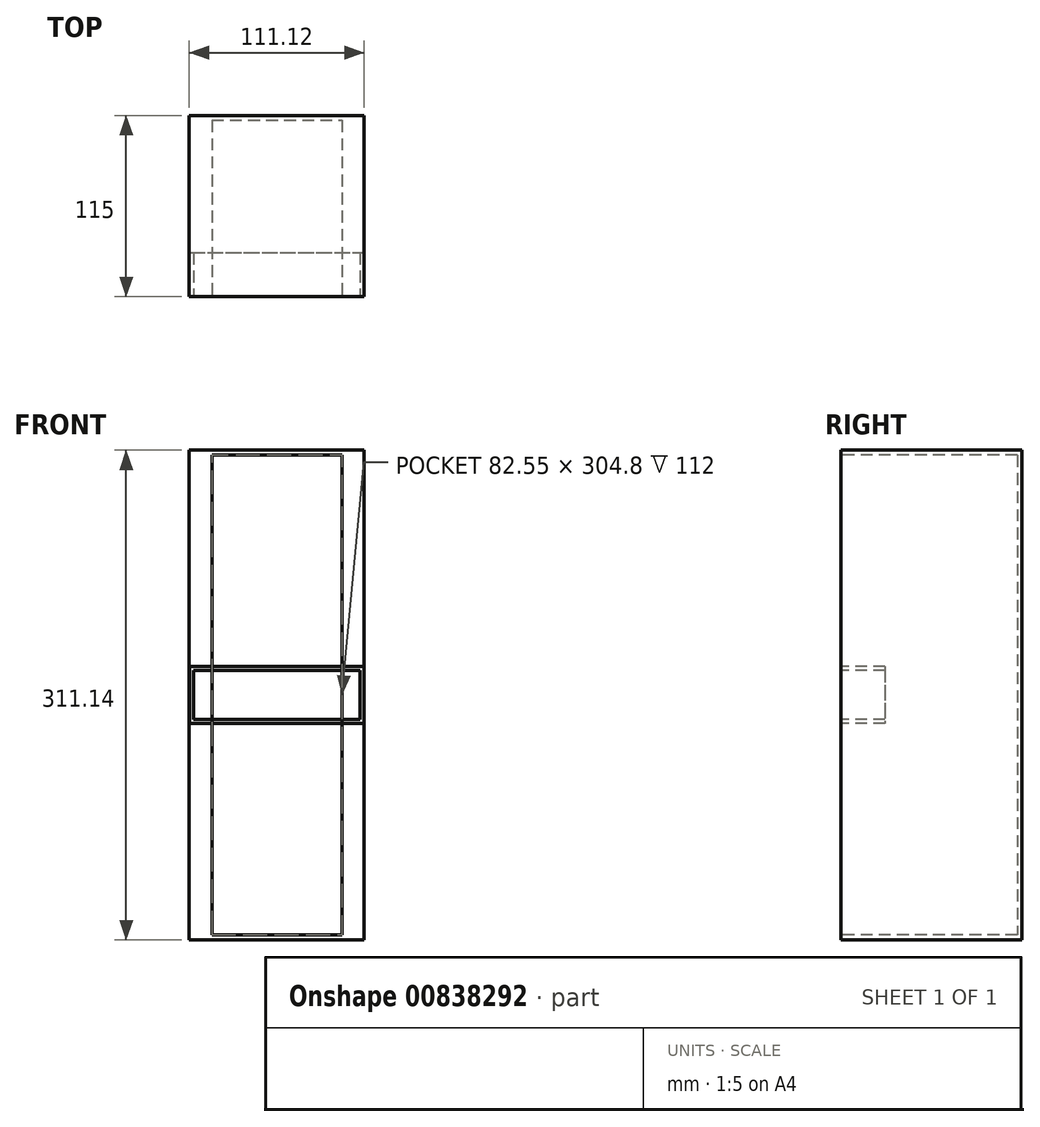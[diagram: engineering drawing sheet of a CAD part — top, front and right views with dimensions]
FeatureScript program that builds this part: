
annotation { "Feature Type Name" : "Feature", "Feature Type Description" : "" }
export const myFeature = defineFeature(function(context is Context, id is Id, definition is map)
    precondition{}
    {
        {
            var Q0;
            Q0=qCreatedBy(makeId("Front.planeOp"),FACE);
            var sketch = newSketch(context, id + "F0", { "sketchPlane" : qUnion([Q0])});
            skLineSegment(sketch, "E0.bottom", {"start": v(-55.56, 155.58) * mm, "end": v(55.56, 155.58) * mm});
            skLineSegment(sketch, "E0.top", {"start": v(-55.56, -155.58) * mm, "end": v(55.56, -155.58) * mm});
            skLineSegment(sketch, "E0.left", {"start": v(-55.56, 155.58) * mm, "end": v(-55.56, -155.58) * mm});
            skLineSegment(sketch, "E0.right", {"start": v(55.56, 155.58) * mm, "end": v(55.56, -155.58) * mm});
            skPoint(sketch, "E0.middle", {"position": v(0, 0) * mm});
            skSolve(sketch);
        }
        {
            var Q0;
            Q0=qCreatedBy(makeId("Front.planeOp"),FACE);
            var sketch = newSketch(context, id + "F1", { "sketchPlane" : qUnion([Q0])});
            skLineSegment(sketch, "E1.bottom", {"start": v(-41.28, 152.4) * mm, "end": v(41.27, 152.4) * mm});
            skLineSegment(sketch, "E1.top", {"start": v(-41.27, -152.4) * mm, "end": v(41.28, -152.4) * mm});
            skLineSegment(sketch, "E1.left", {"start": v(-41.28, 152.4) * mm, "end": v(-41.27, -152.4) * mm});
            skLineSegment(sketch, "E1.right", {"start": v(41.27, 152.4) * mm, "end": v(41.28, -152.4) * mm});
            skPoint(sketch, "E1.middle", {"position": v(0, 0) * mm});
            skSolve(sketch);
        }
        {
            var Q0;
            Q0=makeQuery(id+"F0.imprint","IMPRINT",FACE,{"disambiguationData":[TD([[makeQuery(id+"F0.imprint","IMPRINT",EDGE,{"derivedFrom":sQuery(id+"F0.wireOp",EDGE,"E0.bottom")}),-1.0]])]});
            var Q1;
            Q1=makeQuery(id+"F1.imprint","IMPRINT",FACE,{"disambiguationData":[TD([[makeQuery(id+"F1.imprint","IMPRINT",EDGE,{"derivedFrom":sQuery(id+"F1.wireOp",EDGE,"E1.bottom")}),-1.0]])]});
            extrude(context, id + "F2", {"entities" : qUnion([Q0, Q1]), "depth" : -115 * mm, "offsetDistance" : 25.4 * mm});
        }
        {
            var Q0;
            Q0 = qSketchRegion(id + "F1", true);
            extrude(context, id + "F3", {"entities" : qUnion([Q0]), "operationType" : NewBodyOperationType.REMOVE, "depth" : -112 * mm, "offsetDistance" : 25.4 * mm});
        }
        {
            var Q0;
            Q0=qCreatedBy(makeId("Front.planeOp"),FACE);
            var sketch = newSketch(context, id + "F4", { "sketchPlane" : qUnion([Q0])});
            skLineSegment(sketch, "E2.bottom", {"start": v(-55.5, 18) * mm, "end": v(55.5, 18) * mm});
            skLineSegment(sketch, "E2.top", {"start": v(-55.5, -18) * mm, "end": v(55.5, -18) * mm});
            skLineSegment(sketch, "E2.left", {"start": v(-55.5, 18) * mm, "end": v(-55.5, -18) * mm});
            skLineSegment(sketch, "E2.right", {"start": v(55.5, 18) * mm, "end": v(55.5, -18) * mm});
            skPoint(sketch, "E2.middle", {"position": v(0, 0) * mm});
            skSolve(sketch);
        }
        {
            var Q0;
            Q0 = qSketchRegion(id + "F4", true);
            extrude(context, id + "F5", {"entities" : qUnion([Q0]), "depth" : -28 * mm, "offsetDistance" : 25.4 * mm});
        }
        {
            var Q0;
            Q0=qCreatedBy(makeId("Front.planeOp"),FACE);
            var sketch = newSketch(context, id + "F6", { "sketchPlane" : qUnion([Q0])});
            skLineSegment(sketch, "E3.bottom", {"start": v(-53, 15.5) * mm, "end": v(53, 15.5) * mm});
            skLineSegment(sketch, "E3.top", {"start": v(-53, -15.5) * mm, "end": v(53, -15.5) * mm});
            skLineSegment(sketch, "E3.left", {"start": v(-53, 15.5) * mm, "end": v(-53, -15.5) * mm});
            skLineSegment(sketch, "E3.right", {"start": v(53, 15.5) * mm, "end": v(53, -15.5) * mm});
            skPoint(sketch, "E3.middle", {"position": v(0, 0) * mm});
            skSolve(sketch);
        }
        {
            var Q0;
            Q0 = qSketchRegion(id + "F6", true);
            extrude(context, id + "F7", {"entities" : qUnion([Q0]), "depth" : -28 * mm, "offsetDistance" : 25.4 * mm});
        }
        {
            var Q0;
            Q0=makeQuery(id+"F2.opExtrude","SWEPT_BODY",BODY,{"disambiguationData":[OSD([sQuery(id+"F1.wireOp",EDGE,"E1.bottom"),sQuery(id+"F1.wireOp",EDGE,"E1.top"),sQuery(id+"F1.wireOp",EDGE,"E1.left"),sQuery(id+"F1.wireOp",EDGE,"E1.right")])]});
            deleteBodies(context, id + "F8", {"entities" : qUnion([Q0])});
        }
    });
